# Revit family: TakeUp Tables
name_source: partatom
category: Furniture
revit_build: Autodesk Revit 2016 (Build: 20160525_1230(x64)
units: mm (PartAtom-declared; Revit-internal decimal feet)

## family parameters
Always vertical = Yes
Cut with Voids When Loaded = No
OmniClass Number = 23.40.00.00
OmniClass Title = Equipment and Furnishings
Room Calculation Point = No
Shared = No
Work Plane-Based = No

## types (5) — shared parameters
Assembly Code = E2020200
Foot = Gresham - Black Plastic
Manufacturer = Gresham Office Funiture
Model = TAKE UP
Range = SEATING
Seat = Gresham - Grey Fabric
Top = Gresham - White MFC
URL = www.gof.co.uk

## per-type parameters (varying)
| type | Seat (Visibility) | Width |
| TKU55 | Yes | 500 mm |
| TKU58 | Yes | 800 mm  [stored 2.62467 ft] |
| TKU58T | No | 800 mm  [stored 2.62467 ft] |
| TKU516T | No | 1600 mm |
| TKU516 | Yes | 1600 mm |

note: column(s) folded — value = type name in every type: Product Code

note: [stored X ft] marks values corroborated as IEEE doubles in the binary element streams (Revit-internal decimal feet)

## geometry (parser evidence)
native form markers: Sweep x3
no freeform markers — native parametric forms only
